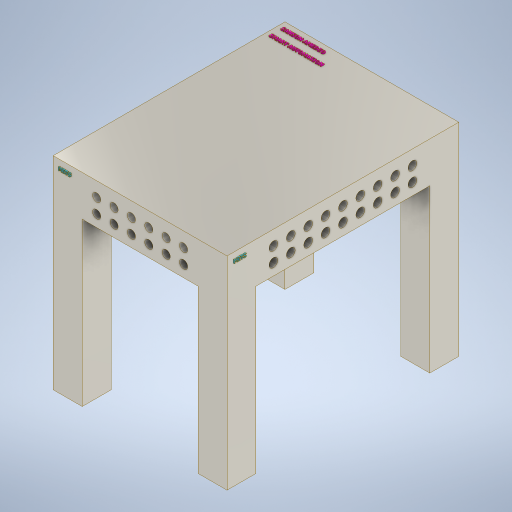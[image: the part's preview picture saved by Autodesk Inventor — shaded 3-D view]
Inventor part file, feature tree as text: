
AUTODESK INVENTOR PART (.ipt)
format: ipt  version: 2023 (Build 270158000, 158)  size: 1,108,992 bytes
history: native  units: mm
features: extrude x8, sketch x4, pattern_linear x2
ambient origin geometry x8: Origin, YZ Plane, XZ Plane, XY Plane, X Axis, Y Axis, Z Axis, Center Point
bodies: Body1 (feature_tree)
feature tree (14):
  sketch  "Schizzo1"
  extrude  "Estrusione5"  Depth=350.0mm TaperAngle=0.0deg
  extrude  "Estrusione6"  Depth=340.0mm TaperAngle=0.0deg
  extrude  "Estrusione7"  Depth=280.0mm TaperAngle=0.0deg
  sketch  "Schizzo6"
  extrude  "Estrusione9"  Depth=400.0mm
  pattern_linear  "Serie rettangolare1"  Count1=30  [1 undecoded]
  sketch  "Schizzo7"
  extrude  "Estrusione10"  Depth=50.0mm
  pattern_linear  "Serie rettangolare2"  Spacing1=15.0mm  [1 undecoded]
  extrude  "Estrusione11"  Depth=30.0mm
  extrude  "Estrusione12"  Depth=15.0mm
  extrude  "Estrusione13"  TaperAngle=0.0deg  [1 undecoded]
  sketch  "Schizzo9"
note: 3 required parameter values undecoded (feature->parameter linkage not recoverable at this tier; creation-order binding heuristic only, values carry confidence <= 0.55)
